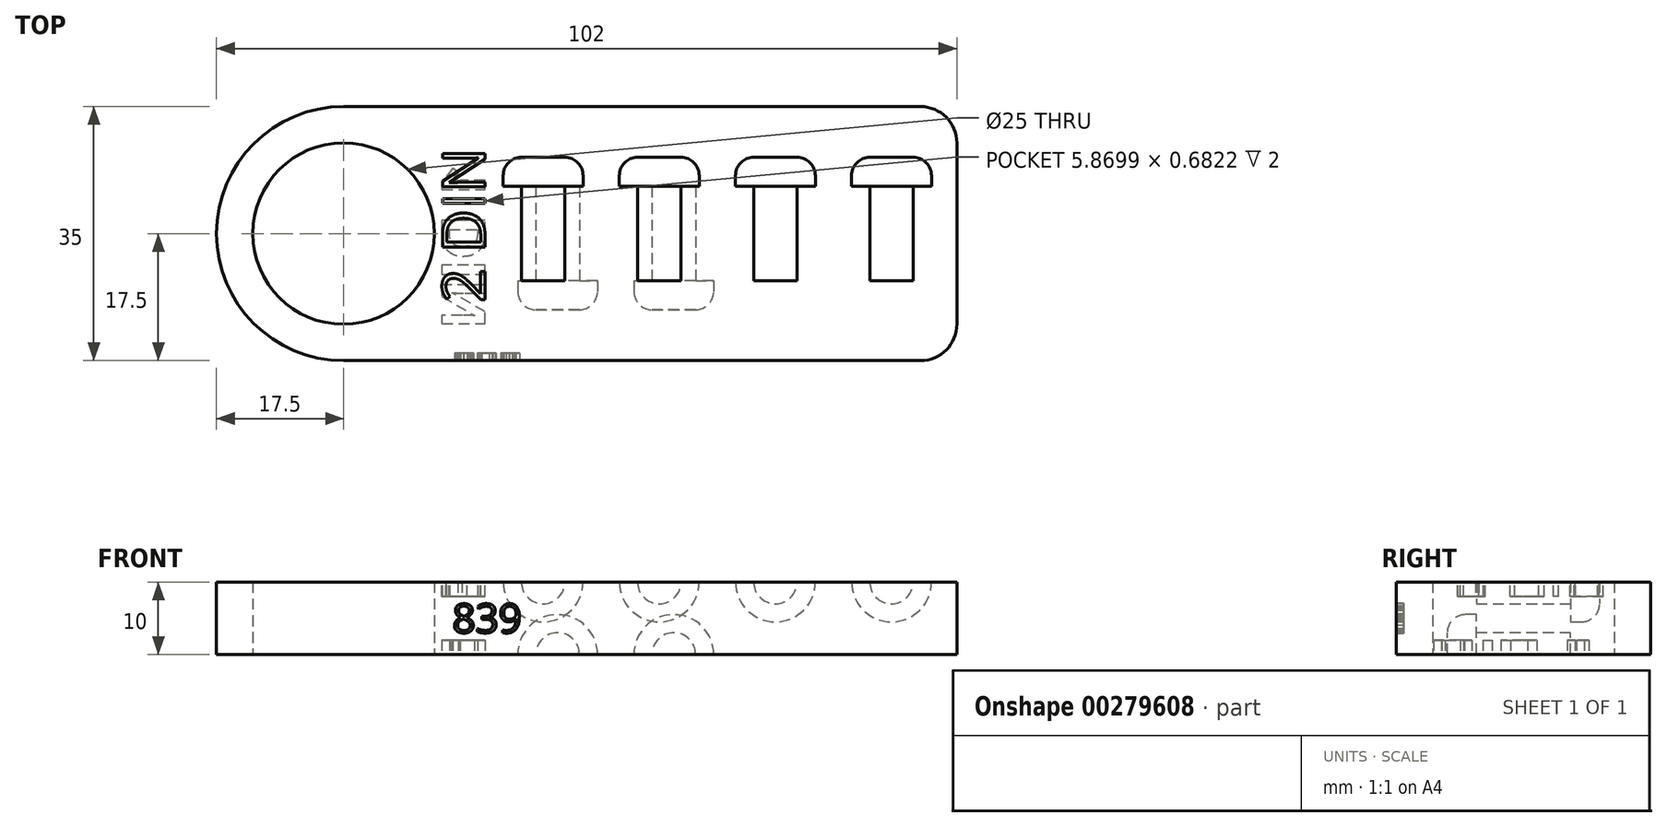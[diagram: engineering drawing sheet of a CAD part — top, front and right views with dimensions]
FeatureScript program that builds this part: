
annotation { "Feature Type Name" : "Feature", "Feature Type Description" : "" }
export const myFeature = defineFeature(function(context is Context, id is Id, definition is map)
    precondition{}
    {
        {
            var Q0;
            Q0=qCreatedBy(makeId("Top.planeOp"),FACE);
            var sketch = newSketch(context, id + "F0", { "sketchPlane" : qUnion([Q0])});
            skLineSegment(sketch, "E0.bottom", {"start": v(17.5, 0) * mm, "end": v(97, 0) * mm});
            skLineSegment(sketch, "E0.top", {"start": v(17.5, 35) * mm, "end": v(97, 35) * mm});
            skLineSegment(sketch, "E0.left", {"start": v(0, 17.5) * mm, "end": v(0, 17.5) * mm});
            skLineSegment(sketch, "E0.right", {"start": v(102, 5) * mm, "end": v(102, 30) * mm});
            skLineSegment(sketch, "E1.bottom", {"start": v(0, 0) * mm, "end": v(17.5, 0) * mm, "construction": true});
            skLineSegment(sketch, "E1.top", {"start": v(0, 17.5) * mm, "end": v(17.5, 17.5) * mm, "construction": true});
            skLineSegment(sketch, "E1.left", {"start": v(0, 0) * mm, "end": v(0, 17.5) * mm, "construction": true});
            skLineSegment(sketch, "E1.right", {"start": v(17.5, 0) * mm, "end": v(17.5, 17.5) * mm, "construction": true});
            skCircle(sketch, "E2", {"center": v(17.5, 17.5) * mm, "radius": 12.5 * mm});
            skPoint(sketch, "E3.visualSharp", {"position": v(0, 0) * mm});
            skArc(sketch, "E3.filletArc", {"start": v(0, 17.5) * mm, "mid": v(5.13, 5.13) * mm, "end": v(17.5, 0) * mm});
            skPoint(sketch, "E4.visualSharp", {"position": v(0, 35) * mm});
            skArc(sketch, "E4.filletArc", {"start": v(17.5, 35) * mm, "mid": v(5.13, 29.87) * mm, "end": v(0, 17.5) * mm});
            skPoint(sketch, "E5.visualSharp", {"position": v(102, 35) * mm});
            skArc(sketch, "E5.filletArc", {"start": v(102, 30) * mm, "mid": v(100.54, 33.54) * mm, "end": v(97, 35) * mm});
            skPoint(sketch, "E6.visualSharp", {"position": v(102, 0) * mm});
            skArc(sketch, "E6.filletArc", {"start": v(97, 0) * mm, "mid": v(100.54, 1.46) * mm, "end": v(102, 5) * mm});
            skSolve(sketch);
        }
        {
            var Q0;
            Q0=makeQuery(id+"F0.imprint","IMPRINT",FACE,{"disambiguationData":[TD([[makeQuery(id+"F0.imprint","IMPRINT",EDGE,{"derivedFrom":sQuery(id+"F0.wireOp",EDGE,"E0.bottom")}),1.0]])]});
            extrude(context, id + "F1", {"entities" : qUnion([Q0]), "depth" : 10 * mm});
        }
        {
            var Q0;
            Q0=makeQuery(id+"F1.opExtrude","CAP_FACE",FACE,{"disambiguationData":[OSD([sQuery(id+"F0.wireOp",EDGE,"E0.bottom"),sQuery(id+"F0.wireOp",EDGE,"E0.top"),sQuery(id+"F0.wireOp",EDGE,"E0.right"),sQuery(id+"F0.wireOp",EDGE,"E2"),sQuery(id+"F0.wireOp",EDGE,"E3.filletArc"),sQuery(id+"F0.wireOp",EDGE,"E4.filletArc"),sQuery(id+"F0.wireOp",EDGE,"E5.filletArc"),sQuery(id+"F0.wireOp",EDGE,"E6.filletArc")])],"isStart":false});
            var sketch = newSketch(context, id + "F2", { "sketchPlane" : qUnion([Q0])});
            skLineSegment(sketch, "E7.bottom", {"start": v(0, 0) * mm, "end": v(45, 0) * mm, "construction": true});
            skLineSegment(sketch, "E7.top", {"start": v(0, 11) * mm, "end": v(45, 11) * mm, "construction": true});
            skLineSegment(sketch, "E7.left", {"start": v(0, 0) * mm, "end": v(0, 11) * mm, "construction": true});
            skLineSegment(sketch, "E7.right", {"start": v(45, 0) * mm, "end": v(45, 11) * mm, "construction": true});
            skLineSegment(sketch, "E8.bottom", {"start": v(45, 11) * mm, "end": v(48, 11) * mm});
            skLineSegment(sketch, "E8.left", {"start": v(45, 11) * mm, "end": v(45, 24) * mm});
            skLineSegment(sketch, "E8.right", {"start": v(48, 11) * mm, "end": v(48, 24) * mm});
            skLineSegment(sketch, "E9.bottom", {"start": v(48, 24) * mm, "end": v(50.5, 24) * mm});
            skLineSegment(sketch, "E9.top", {"start": v(45, 28) * mm, "end": v(48, 28) * mm});
            skLineSegment(sketch, "E9.left", {"start": v(45, 24) * mm, "end": v(45, 28) * mm});
            skLineSegment(sketch, "E9.right", {"start": v(50.5, 24) * mm, "end": v(50.5, 25.5) * mm});
            skPoint(sketch, "E10.visualSharp", {"position": v(50.5, 28) * mm});
            skArc(sketch, "E10.filletArc", {"start": v(50.5, 25.5) * mm, "mid": v(49.77, 27.27) * mm, "end": v(48, 28) * mm});
            skLineSegment(sketch, "E11", {"start": v(45, 11) * mm, "end": v(61, 11) * mm, "construction": true});
            skLineSegment(sketch, "E12", {"start": v(61, 11) * mm, "end": v(77, 11) * mm, "construction": true});
            skLineSegment(sketch, "E13", {"start": v(77, 11) * mm, "end": v(93, 11) * mm, "construction": true});
            skLineSegment(sketch, "E14.bottom", {"start": v(93, 11) * mm, "end": v(96, 11) * mm});
            skLineSegment(sketch, "E14.left", {"start": v(93, 11) * mm, "end": v(93, 24) * mm});
            skLineSegment(sketch, "E14.right", {"start": v(96, 11) * mm, "end": v(96, 24) * mm});
            skLineSegment(sketch, "E15.bottom", {"start": v(96, 24) * mm, "end": v(98.5, 24) * mm});
            skLineSegment(sketch, "E15.top", {"start": v(93, 28) * mm, "end": v(96, 28) * mm});
            skLineSegment(sketch, "E15.left", {"start": v(93, 24) * mm, "end": v(93, 28) * mm});
            skLineSegment(sketch, "E15.right", {"start": v(98.5, 24) * mm, "end": v(98.5, 25.5) * mm});
            skPoint(sketch, "E16.visualSharp", {"position": v(98.5, 28) * mm});
            skArc(sketch, "E16.filletArc", {"start": v(98.5, 25.5) * mm, "mid": v(97.77, 27.27) * mm, "end": v(96, 28) * mm});
            skLineSegment(sketch, "E17.bottom", {"start": v(77, 11) * mm, "end": v(80, 11) * mm});
            skLineSegment(sketch, "E17.left", {"start": v(77, 11) * mm, "end": v(77, 24) * mm});
            skLineSegment(sketch, "E17.right", {"start": v(80, 11) * mm, "end": v(80, 24) * mm});
            skLineSegment(sketch, "E18.bottom", {"start": v(80, 24) * mm, "end": v(82.5, 24) * mm});
            skLineSegment(sketch, "E18.top", {"start": v(77, 28) * mm, "end": v(80, 28) * mm});
            skLineSegment(sketch, "E18.left", {"start": v(77, 24) * mm, "end": v(77, 28) * mm});
            skLineSegment(sketch, "E18.right", {"start": v(82.5, 24) * mm, "end": v(82.5, 25.5) * mm});
            skPoint(sketch, "E19.visualSharp", {"position": v(82.5, 28) * mm});
            skArc(sketch, "E19.filletArc", {"start": v(82.5, 25.5) * mm, "mid": v(81.77, 27.27) * mm, "end": v(80, 28) * mm});
            skLineSegment(sketch, "E20.bottom", {"start": v(61, 11) * mm, "end": v(64, 11) * mm});
            skLineSegment(sketch, "E20.left", {"start": v(61, 11) * mm, "end": v(61, 24) * mm});
            skLineSegment(sketch, "E20.right", {"start": v(64, 11) * mm, "end": v(64, 24) * mm});
            skLineSegment(sketch, "E21.bottom", {"start": v(64, 24) * mm, "end": v(66.5, 24) * mm});
            skLineSegment(sketch, "E21.top", {"start": v(61, 28) * mm, "end": v(64, 28) * mm});
            skLineSegment(sketch, "E21.left", {"start": v(61, 24) * mm, "end": v(61, 28) * mm});
            skLineSegment(sketch, "E21.right", {"start": v(66.5, 24) * mm, "end": v(66.5, 25.5) * mm});
            skPoint(sketch, "E22.visualSharp", {"position": v(66.5, 28) * mm});
            skArc(sketch, "E22.filletArc", {"start": v(66.5, 25.5) * mm, "mid": v(65.77, 27.27) * mm, "end": v(64, 28) * mm});
            skText(sketch, "E23", { "text": "2 DIN", "fontName": "OpenSans-Regular.ttf"});
            skLineSegment(sketch, "E24", {"start": v(0, 11) * mm, "end": v(37, 11) * mm, "construction": true});
            skLineSegment(sketch, "E25", {"start": v(37, 11) * mm, "end": v(37, 8) * mm, "construction": true});
            const initialGuessF2  = {"E23": [0.037, 0.008, 0, 1, 0.00592]};
            skSetInitialGuess(sketch, initialGuessF2);
            skSolve(sketch);
        }
        {
            var Q0;
            Q0=makeQuery(id+"F2.imprint","IMPRINT",FACE,{"disambiguationData":[TD([[makeQuery(id+"F2.imprint","IMPRINT",EDGE,{"derivedFrom":sQuery(id+"F2.wireOp",EDGE,"E8.bottom")}),1.0]])]});
            var Q1;
            Q1=sQuery(id+"F2.wireOp",EDGE,"E8.left");
            revolve(context, id + "F3", {"operationType" : NewBodyOperationType.REMOVE, "entities" : qUnion([Q0]), "axis" : qUnion([Q1]), "revolveType" : RevolveType.FULL, "oppositeDirection" : true});
        }
        {
            var Q0;
            Q0=makeQuery(id+"F2.imprint","IMPRINT",FACE,{"disambiguationData":[TD([[makeQuery(id+"F2.imprint","IMPRINT",EDGE,{"derivedFrom":sQuery(id+"F2.wireOp",EDGE,"E20.bottom")}),1.0]])]});
            var Q1;
            Q1=sQuery(id+"F2.wireOp",EDGE,"E20.left");
            revolve(context, id + "F4", {"operationType" : NewBodyOperationType.REMOVE, "entities" : qUnion([Q0]), "axis" : qUnion([Q1]), "revolveType" : RevolveType.FULL, "oppositeDirection" : true});
        }
        {
            var Q0;
            Q0=makeQuery(id+"F2.imprint","IMPRINT",FACE,{"disambiguationData":[TD([[makeQuery(id+"F2.imprint","IMPRINT",EDGE,{"derivedFrom":sQuery(id+"F2.wireOp",EDGE,"E17.bottom")}),1.0]])]});
            var Q1;
            Q1=sQuery(id+"F2.wireOp",EDGE,"E17.left");
            revolve(context, id + "F5", {"operationType" : NewBodyOperationType.REMOVE, "entities" : qUnion([Q0]), "axis" : qUnion([Q1]), "revolveType" : RevolveType.FULL, "oppositeDirection" : true});
        }
        {
            var Q0;
            Q0=makeQuery(id+"F2.imprint","IMPRINT",FACE,{"disambiguationData":[TD([[makeQuery(id+"F2.imprint","IMPRINT",EDGE,{"derivedFrom":sQuery(id+"F2.wireOp",EDGE,"E14.bottom")}),1.0]])]});
            var Q1;
            Q1=sQuery(id+"F2.wireOp",EDGE,"E14.left");
            revolve(context, id + "F6", {"operationType" : NewBodyOperationType.REMOVE, "entities" : qUnion([Q0]), "axis" : qUnion([Q1]), "revolveType" : RevolveType.FULL, "oppositeDirection" : true});
        }
        {
            var Q0;
            Q0=makeQuery(id+"F2.imprint","IMPRINT",FACE,{"disambiguationData":[TD([[makeQuery(id+"F2.imprint","IMPRINT",EDGE,{"derivedFrom":sQuery(id+"F2.wireOp",EDGE,"E23.sketch_text.stroke-0")}),-1.0]])]});
            var Q1;
            Q1=makeQuery(id+"F2.imprint","IMPRINT",FACE,{"disambiguationData":[TD([[makeQuery(id+"F2.imprint","IMPRINT",EDGE,{"derivedFrom":sQuery(id+"F2.wireOp",EDGE,"E23.sketch_text.stroke-20")}),-1.0]])]});
            var Q2;
            Q2=makeQuery(id+"F2.imprint","IMPRINT",FACE,{"disambiguationData":[TD([[makeQuery(id+"F2.imprint","IMPRINT",EDGE,{"derivedFrom":sQuery(id+"F2.wireOp",EDGE,"E23.sketch_text.stroke-34")}),-1.0]])]});
            var Q3;
            Q3=makeQuery(id+"F2.imprint","IMPRINT",FACE,{"disambiguationData":[TD([[makeQuery(id+"F2.imprint","IMPRINT",EDGE,{"derivedFrom":sQuery(id+"F2.wireOp",EDGE,"E23.sketch_text.stroke-38")}),-1.0]])]});
            extrude(context, id + "F7", {"entities" : qUnion([Q0, Q1, Q2, Q3]), "operationType" : NewBodyOperationType.REMOVE, "oppositeDirection" : true, "depth" : 2 * mm});
        }
        {
            var Q0;
            Q0=makeQuery(id+"F1.opExtrude","CAP_FACE",FACE,{"disambiguationData":[OSD([sQuery(id+"F0.wireOp",EDGE,"E0.bottom"),sQuery(id+"F0.wireOp",EDGE,"E0.top"),sQuery(id+"F0.wireOp",EDGE,"E0.right"),sQuery(id+"F0.wireOp",EDGE,"E2"),sQuery(id+"F0.wireOp",EDGE,"E3.filletArc"),sQuery(id+"F0.wireOp",EDGE,"E4.filletArc"),sQuery(id+"F0.wireOp",EDGE,"E5.filletArc"),sQuery(id+"F0.wireOp",EDGE,"E6.filletArc")])],"isStart":true});
            var sketch = newSketch(context, id + "F8", { "sketchPlane" : qUnion([Q0])});
            skLineSegment(sketch, "E26.bottom", {"start": v(0, 0) * mm, "end": v(47, 0) * mm, "construction": true});
            skLineSegment(sketch, "E26.top", {"start": v(0, -24) * mm, "end": v(47, -24) * mm, "construction": true});
            skLineSegment(sketch, "E26.left", {"start": v(0, 0) * mm, "end": v(0, -24) * mm, "construction": true});
            skLineSegment(sketch, "E26.right", {"start": v(47, 0) * mm, "end": v(47, -24) * mm, "construction": true});
            skLineSegment(sketch, "E27", {"start": v(47, -24) * mm, "end": v(63, -24) * mm, "construction": true});
            skLineSegment(sketch, "E28.bottom", {"start": v(47, -24) * mm, "end": v(50, -24) * mm});
            skLineSegment(sketch, "E28.left", {"start": v(47, -24) * mm, "end": v(47, -11) * mm});
            skLineSegment(sketch, "E28.right", {"start": v(50, -24) * mm, "end": v(50, -11) * mm});
            skLineSegment(sketch, "E29.bottom", {"start": v(50, -11) * mm, "end": v(52.5, -11) * mm});
            skLineSegment(sketch, "E29.top", {"start": v(47, -7) * mm, "end": v(50, -7) * mm});
            skLineSegment(sketch, "E29.left", {"start": v(47, -11) * mm, "end": v(47, -7) * mm});
            skLineSegment(sketch, "E29.right", {"start": v(52.5, -11) * mm, "end": v(52.5, -9.5) * mm});
            skPoint(sketch, "E30.visualSharp", {"position": v(52.5, -7) * mm});
            skArc(sketch, "E30.filletArc", {"start": v(52.5, -9.5) * mm, "mid": v(51.77, -7.73) * mm, "end": v(50, -7) * mm});
            skLineSegment(sketch, "E31.bottom", {"start": v(63, -24) * mm, "end": v(66, -24) * mm});
            skLineSegment(sketch, "E31.left", {"start": v(63, -24) * mm, "end": v(63, -11) * mm});
            skLineSegment(sketch, "E31.right", {"start": v(66, -24) * mm, "end": v(66, -11) * mm});
            skLineSegment(sketch, "E32.bottom", {"start": v(66, -11) * mm, "end": v(68.5, -11) * mm});
            skLineSegment(sketch, "E32.top", {"start": v(63, -7) * mm, "end": v(66, -7) * mm});
            skLineSegment(sketch, "E32.left", {"start": v(63, -11) * mm, "end": v(63, -7) * mm});
            skLineSegment(sketch, "E32.right", {"start": v(68.5, -11) * mm, "end": v(68.5, -9.5) * mm});
            skPoint(sketch, "E33.visualSharp", {"position": v(68.5, -7) * mm});
            skArc(sketch, "E33.filletArc", {"start": v(68.5, -9.5) * mm, "mid": v(67.77, -7.73) * mm, "end": v(66, -7) * mm});
            skLineSegment(sketch, "E34", {"start": v(0, -24) * mm, "end": v(37, -24) * mm, "construction": true});
            skLineSegment(sketch, "E35", {"start": v(37, -24) * mm, "end": v(37, -27) * mm, "construction": true});
            skText(sketch, "E36", { "text": "1 DIN", "fontName": "OpenSans-Bold.ttf"});
            const initialGuessF8  = {"E36": [0.037, -0.027, 0, 1, 0.006]};
            skSetInitialGuess(sketch, initialGuessF8);
            skSolve(sketch);
        }
        {
            var Q0;
            Q0=makeQuery(id+"F8.imprint","IMPRINT",FACE,{"disambiguationData":[TD([[makeQuery(id+"F8.imprint","IMPRINT",EDGE,{"derivedFrom":sQuery(id+"F8.wireOp",EDGE,"E36.sketch_text.stroke-0")}),-1.0]])]});
            var Q1;
            Q1=makeQuery(id+"F8.imprint","IMPRINT",FACE,{"disambiguationData":[TD([[makeQuery(id+"F8.imprint","IMPRINT",EDGE,{"derivedFrom":sQuery(id+"F8.wireOp",EDGE,"E36.sketch_text.stroke-10")}),-1.0]])]});
            var Q2;
            Q2=makeQuery(id+"F8.imprint","IMPRINT",FACE,{"disambiguationData":[TD([[makeQuery(id+"F8.imprint","IMPRINT",EDGE,{"derivedFrom":sQuery(id+"F8.wireOp",EDGE,"E36.sketch_text.stroke-22")}),-1.0]])]});
            var Q3;
            Q3=makeQuery(id+"F8.imprint","IMPRINT",FACE,{"disambiguationData":[TD([[makeQuery(id+"F8.imprint","IMPRINT",EDGE,{"derivedFrom":sQuery(id+"F8.wireOp",EDGE,"E36.sketch_text.stroke-26")}),-1.0]])]});
            extrude(context, id + "F9", {"entities" : qUnion([Q0, Q1, Q2, Q3]), "operationType" : NewBodyOperationType.REMOVE, "oppositeDirection" : true, "depth" : 2 * mm});
        }
        {
            var Q0;
            Q0=makeQuery(id+"F8.imprint","IMPRINT",FACE,{"disambiguationData":[TD([[makeQuery(id+"F8.imprint","IMPRINT",EDGE,{"derivedFrom":sQuery(id+"F8.wireOp",EDGE,"E28.bottom")}),1.0]])]});
            var Q1;
            Q1=sQuery(id+"F8.wireOp",EDGE,"E28.left");
            revolve(context, id + "F10", {"operationType" : NewBodyOperationType.REMOVE, "entities" : qUnion([Q0]), "axis" : qUnion([Q1]), "revolveType" : RevolveType.FULL, "oppositeDirection" : true});
        }
        {
            var Q0;
            Q0=makeQuery(id+"F8.imprint","IMPRINT",FACE,{"disambiguationData":[TD([[makeQuery(id+"F8.imprint","IMPRINT",EDGE,{"derivedFrom":sQuery(id+"F8.wireOp",EDGE,"E31.bottom")}),1.0]])]});
            var Q1;
            Q1=sQuery(id+"F8.wireOp",EDGE,"E31.left");
            revolve(context, id + "F11", {"operationType" : NewBodyOperationType.REMOVE, "entities" : qUnion([Q0]), "axis" : qUnion([Q1]), "revolveType" : RevolveType.FULL, "oppositeDirection" : true});
        }
        {
            var Q0;
            Q0=makeQuery(id+"F1.opExtrude","SWEPT_FACE",FACE,{"disambiguationData":[OSD([sQuery(id+"F0.wireOp",EDGE,"E0.bottom")])]});
            var sketch = newSketch(context, id + "F12", { "sketchPlane" : qUnion([Q0])});
            skLineSegment(sketch, "E37.bottom", {"start": v(17.5, 10) * mm, "end": v(32.5, 10) * mm, "construction": true});
            skLineSegment(sketch, "E37.top", {"start": v(17.5, 7) * mm, "end": v(32.5, 7) * mm, "construction": true});
            skLineSegment(sketch, "E37.left", {"start": v(17.5, 10) * mm, "end": v(17.5, 7) * mm, "construction": true});
            skLineSegment(sketch, "E37.right", {"start": v(32.5, 10) * mm, "end": v(32.5, 7) * mm, "construction": true});
            skText(sketch, "E38", { "text": "839\n", "fontName": "OpenSans-Regular.ttf"});
            const initialGuessF12  = {"E38": [0.0325, 0.003, 1, 0, 0.004]};
            skSetInitialGuess(sketch, initialGuessF12);
            skSolve(sketch);
        }
        {
            var Q0;
            Q0 = qSketchRegion(id + "F12", true);
            extrude(context, id + "F13", {"entities" : qUnion([Q0]), "operationType" : NewBodyOperationType.REMOVE, "oppositeDirection" : true, "depth" : 1 * mm});
        }
    });
